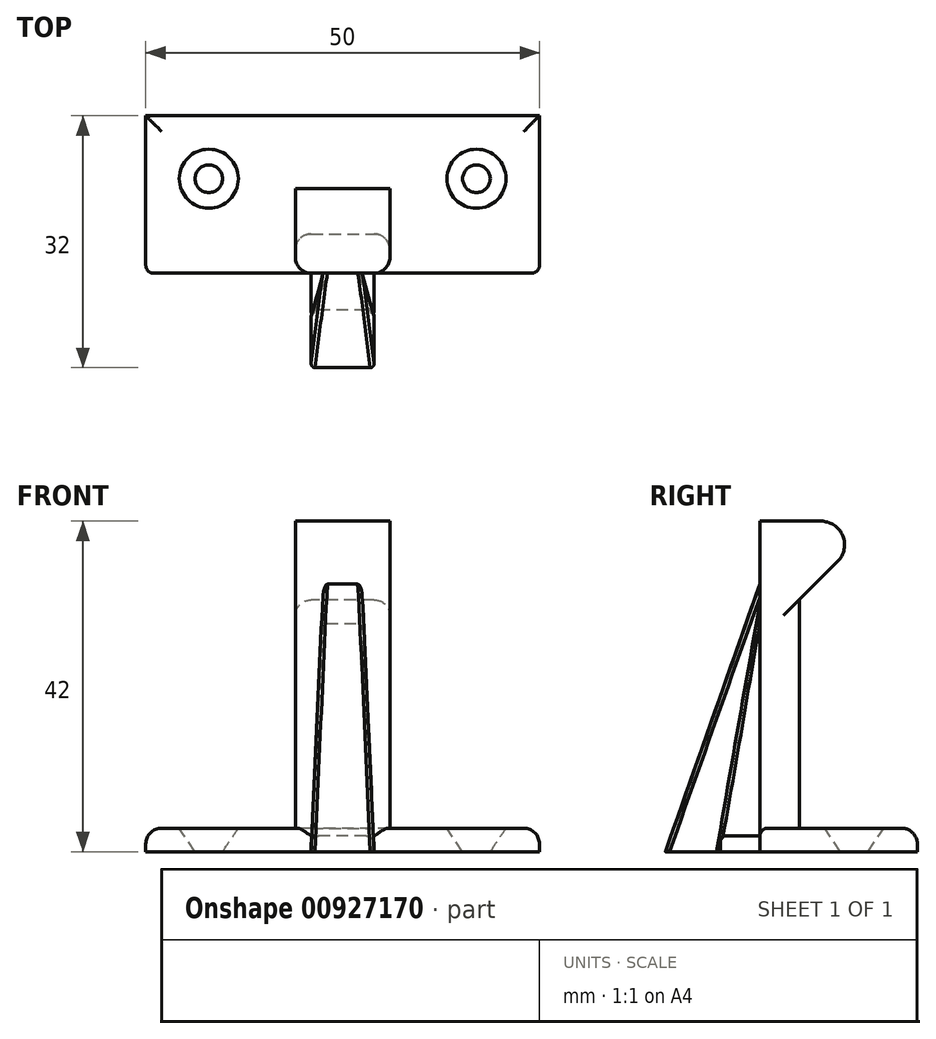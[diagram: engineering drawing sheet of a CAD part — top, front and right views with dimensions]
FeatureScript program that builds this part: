
annotation { "Feature Type Name" : "Feature", "Feature Type Description" : "" }
export const myFeature = defineFeature(function(context is Context, id is Id, definition is map)
    precondition{}
    {
        {
            var Q0;
            Q0=qCreatedBy(makeId("Top.planeOp"),FACE);
            var sketch = newSketch(context, id + "F0", { "sketchPlane" : qUnion([Q0])});
            skLineSegment(sketch, "E0.bottom", {"start": v(25, -10) * mm, "end": v(-25, -10) * mm});
            skLineSegment(sketch, "E0.top", {"start": v(25, 10) * mm, "end": v(-25, 10) * mm});
            skLineSegment(sketch, "E0.left", {"start": v(25, -10) * mm, "end": v(25, 10) * mm});
            skLineSegment(sketch, "E0.right", {"start": v(-25, -10) * mm, "end": v(-25, 10) * mm});
            skPoint(sketch, "E0.middle", {"position": v(0, 0) * mm});
            skLineSegment(sketch, "E1.bottom", {"start": v(-6, -10) * mm, "end": v(6, -10) * mm});
            skLineSegment(sketch, "E1.top", {"start": v(-6, -5) * mm, "end": v(6, -5) * mm});
            skLineSegment(sketch, "E1.left", {"start": v(6, -10) * mm, "end": v(6, -5) * mm});
            skLineSegment(sketch, "E1.right", {"start": v(-6, -10) * mm, "end": v(-6, -5) * mm});
            skPoint(sketch, "E2", {"position": v(0, -5) * mm});
            skCircle(sketch, "E3", {"center": v(-17, 2) * mm, "radius": 1.75 * mm});
            skCircle(sketch, "E4.MirrorC", {"center": v(17, 2) * mm, "radius": 1.75 * mm});
            skLineSegment(sketch, "E5.bottom", {"start": v(-4, -10) * mm, "end": v(4, -10) * mm});
            skLineSegment(sketch, "E5.top", {"start": v(-4, -22) * mm, "end": v(4, -22) * mm});
            skLineSegment(sketch, "E5.left", {"start": v(-4, -10) * mm, "end": v(-4, -22) * mm});
            skLineSegment(sketch, "E5.right", {"start": v(4, -10) * mm, "end": v(4, -22) * mm});
            skPoint(sketch, "E6", {"position": v(0, -10) * mm});
            skLineSegment(sketch, "E7", {"start": v(4, -15) * mm, "end": v(-4, -15) * mm});
            skSolve(sketch);
        }
        {
            var Q0;
            Q0=makeQuery(id+"F0.imprint","IMPRINT",FACE,{"disambiguationData":[TD([[makeQuery(id+"F0.imprint","IMPRINT",EDGE,{"derivedFrom":sQuery(id+"F0.wireOp",EDGE,"E0.top")}),1.0]])]});
            extrude(context, id + "F1", {"entities" : qUnion([Q0]), "depth" : 3 * mm, "offsetDistance" : 25 * mm});
        }
        {
            var Q0;
            Q0=makeQuery(id+"F0.imprint","IMPRINT",FACE,{"disambiguationData":[TD([[makeQuery(id+"F0.imprint","IMPRINT",EDGE,{"derivedFrom":sQuery(id+"F0.wireOp",EDGE,"E1.top")}),-1.0]])]});
            extrude(context, id + "F2", {"entities" : qUnion([Q0]), "operationType" : NewBodyOperationType.ADD, "depth" : 42 * mm, "offsetDistance" : 25 * mm});
        }
        {
            var Q0;
            {var subQ0=sQuery(id+"F0.wireOp",EDGE,"E0.bottom");Q0=makeQuery(id+"F2.boolean.opBoolean","MERGE",FACE,{"derivedFrom":[makeQuery(id+"F1.opExtrude","SWEPT_FACE",FACE,{"disambiguationData":[OSD([subQ0]),TDD([makeQuery(id+"F0.imprint","IMPRINT",EDGE,{"disambiguationData":[TD([[makeQuery(id+"F0.imprint","INTERSECT",VERTEX,{"derivedFrom":[subQ0,sQuery(id+"F0.wireOp",EDGE,"E1.right")]}),-1.0]])],"derivedFrom":subQ0})])]}),makeQuery(id+"F1.opExtrude","SWEPT_FACE",FACE,{"disambiguationData":[OSD([subQ0]),TDD([makeQuery(id+"F0.imprint","IMPRINT",EDGE,{"disambiguationData":[TD([[makeQuery(id+"F0.imprint","INTERSECT",VERTEX,{"derivedFrom":[subQ0,sQuery(id+"F0.wireOp",EDGE,"E0.left")]}),-1.0]])],"derivedFrom":subQ0})])]}),makeQuery(id+"F2.opExtrude","SWEPT_FACE",FACE,{"disambiguationData":[OSD([subQ0])]})]});}
            var sketch = newSketch(context, id + "F3", { "sketchPlane" : qUnion([Q0])});
            skLineSegment(sketch, "E8.bottom", {"start": v(-2.5, 34) * mm, "end": v(2.5, 34) * mm});
            skLineSegment(sketch, "E8.top", {"start": v(-2.5, 29) * mm, "end": v(2.5, 29) * mm});
            skLineSegment(sketch, "E8.left", {"start": v(-2.5, 34) * mm, "end": v(-2.5, 29) * mm});
            skLineSegment(sketch, "E8.right", {"start": v(2.5, 34) * mm, "end": v(2.5, 29) * mm});
            skLineSegment(sketch, "E9", {"start": v(0, 42) * mm, "end": v(0, 34) * mm, "construction": true});
            skSolve(sketch);
        }
        {
            var Q0;
            {var subQ5=sQuery(id+"F0.wireOp",EDGE,"E7");Q0=makeQuery(id+"F0.imprint","IMPRINT",FACE,{"disambiguationData":[TD([[makeQuery(id+"F0.imprint","IMPRINT",EDGE,{"derivedFrom":subQ5}),-1.0]])]});}
            extrude(context, id + "F4", {"entities" : qUnion([Q0]), "operationType" : NewBodyOperationType.ADD, "depth" : 2 * mm, "offsetDistance" : 25 * mm});
        }
        {
            var Q1;
            {var subQ0=sQuery(id+"F0.wireOp",EDGE,"E5.top");Q1=makeQuery(id+"F0.imprint","IMPRINT",FACE,{"disambiguationData":[TD([[makeQuery(id+"F0.imprint","IMPRINT",EDGE,{"derivedFrom":subQ0}),1.0]])]});}
            var Q2;
            Q2=makeQuery(id+"F3.imprint","IMPRINT",FACE,{"disambiguationData":[TD([[makeQuery(id+"F3.imprint","IMPRINT",EDGE,{"derivedFrom":sQuery(id+"F3.wireOp",EDGE,"E8.bottom")}),-1.0]])]});
            loft(context, id + "F5", {"operationType" : NewBodyOperationType.ADD, "sheetProfilesArray" : [{ "sheetProfileEntities" : qUnion([Q1]) }, { "sheetProfileEntities" : qUnion([Q2]) }]});
        }
        {
            var Q0;
            Q0=makeQuery(id+"F2.opExtrude","SWEPT_FACE",FACE,{"disambiguationData":[OSD([sQuery(id+"F0.wireOp",EDGE,"E1.top")])]});
            var sketch = newSketch(context, id + "F6", { "sketchPlane" : qUnion([Q0])});
            skLineSegment(sketch, "E10", {"start": v(-6, 32) * mm, "end": v(6, 32) * mm});
            skSolve(sketch);
        }
        {
            var Q0;
            {var subQ0=sQuery(id+"F6.wireOp",EDGE,"E10");Q0=makeQuery(id+"F6.imprint","IMPRINT",FACE,{"disambiguationData":[TD([[makeQuery(id+"F6.imprint","IMPRINT",EDGE,{"derivedFrom":subQ0}),1.0]])]});}
            extrude(context, id + "F7", {"entities" : qUnion([Q0]), "operationType" : NewBodyOperationType.ADD, "depth" : 10 * mm, "offsetDistance" : 25 * mm});
        }
        {
            var Q0;
            Q0=makeQuery(id+"F7.opExtrude","CAP_EDGE",EDGE,{"disambiguationData":[OSD([sQuery(id+"F6.wireOp",EDGE,"E10")])],"isStart":false});
            chamfer(context, id + "F8", {"entities" : qUnion([Q0]), "width" : 10 * mm, "tangentPropagation" : true});
        }
        {
            var Q0;
            Q0=makeQuery(id+"F1.opExtrude","CAP_EDGE",EDGE,{"disambiguationData":[OSD([sQuery(id+"F0.wireOp",EDGE,"E3")])],"isStart":false});
            var Q1;
            Q1=makeQuery(id+"F1.opExtrude","CAP_EDGE",EDGE,{"disambiguationData":[OSD([sQuery(id+"F0.wireOp",EDGE,"E4.MirrorC")])],"isStart":false});
            chamfer(context, id + "F9", {"entities" : qUnion([Q0, Q1]), "chamferType" : ChamferType.TWO_OFFSETS, "width1" : 3 * mm, "oppositeDirection" : false, "width2" : 2 * mm, "tangentPropagation" : true});
        }
        {
            var Q0;
            {var subQ0=sQuery(id+"F0.wireOp",EDGE,"E1.top");Q0=makeQuery(id+"F8.opChamfer","BLEND_EDGE",EDGE,{"blendedFrom":[makeQuery(id+"F7.opExtrude","CAP_EDGE",EDGE,{"disambiguationData":[OSD([sQuery(id+"F6.wireOp",EDGE,"E10")])],"isStart":false}),makeQuery(id+"F7.boolean.opBoolean","MERGE",FACE,{"derivedFrom":[makeQuery(id+"F2.opExtrude","CAP_FACE",FACE,{"disambiguationData":[OSD([sQuery(id+"F0.wireOp",EDGE,"E0.bottom"),subQ0,sQuery(id+"F0.wireOp",EDGE,"E1.left"),sQuery(id+"F0.wireOp",EDGE,"E1.right")])],"isStart":false}),makeQuery(id+"F7.opExtrude","SWEPT_FACE",FACE,{"disambiguationData":[OSD([subQ0])]})]})],"blendedInto":[makeQuery(id+"F7.boolean.opBoolean","MERGE",FACE,{"derivedFrom":[makeQuery(id+"F2.opExtrude","CAP_FACE",FACE,{"disambiguationData":[OSD([sQuery(id+"F0.wireOp",EDGE,"E0.bottom"),subQ0,sQuery(id+"F0.wireOp",EDGE,"E1.left"),sQuery(id+"F0.wireOp",EDGE,"E1.right")])],"isStart":false}),makeQuery(id+"F7.opExtrude","SWEPT_FACE",FACE,{"disambiguationData":[OSD([subQ0])]})]})]});}
            fillet(context, id + "F10", {"entities" : qUnion([Q0]), "radius" : 3 * mm, "tangentPropagation" : true, "allowEdgeOverflow" : false});
        }
        {
            var Q0;
            Q0=makeQuery(id+"F2.opExtrude","SWEPT_EDGE",EDGE,{"disambiguationData":[OSD([sQuery(id+"F0.wireOp",EDGE,"E1.top"),sQuery(id+"F0.wireOp",EDGE,"E1.left")])]});
            var Q1;
            Q1=makeQuery(id+"F2.opExtrude","SWEPT_EDGE",EDGE,{"disambiguationData":[OSD([sQuery(id+"F0.wireOp",EDGE,"E1.top"),sQuery(id+"F0.wireOp",EDGE,"E1.right")])]});
            var Q2;
            Q2=makeQuery(id+"F2.opExtrude","SWEPT_EDGE",EDGE,{"disambiguationData":[OSD([sQuery(id+"F0.wireOp",EDGE,"E0.bottom"),sQuery(id+"F0.wireOp",EDGE,"E1.left")])]});
            var Q3;
            Q3=makeQuery(id+"F2.opExtrude","SWEPT_EDGE",EDGE,{"disambiguationData":[OSD([sQuery(id+"F0.wireOp",EDGE,"E0.bottom"),sQuery(id+"F0.wireOp",EDGE,"E1.right")])]});
            fillet(context, id + "F11", {"entities" : qUnion([Q0, Q1, Q2, Q3]), "radius" : 2 * mm, "tangentPropagation" : true, "allowEdgeOverflow" : false});
        }
        {
            var Q0;
            Q0=makeQuery(id+"F1.opExtrude","CAP_EDGE",EDGE,{"disambiguationData":[OSD([sQuery(id+"F0.wireOp",EDGE,"E0.top")])],"isStart":false});
            var Q1;
            Q1=makeQuery(id+"F1.opExtrude","CAP_EDGE",EDGE,{"disambiguationData":[OSD([sQuery(id+"F0.wireOp",EDGE,"E0.right")])],"isStart":false});
            var Q2;
            Q2=makeQuery(id+"F1.opExtrude","CAP_EDGE",EDGE,{"disambiguationData":[OSD([sQuery(id+"F0.wireOp",EDGE,"E0.left")])],"isStart":false});
            fillet(context, id + "F12", {"entities" : qUnion([Q0, Q1, Q2]), "radius" : 2 * mm, "tangentPropagation" : true, "allowEdgeOverflow" : false});
        }
        {
            var Q0;
            {var subQ0=sQuery(id+"F0.wireOp",EDGE,"E0.bottom");Q0=makeQuery(id+"F1.opExtrude","CAP_EDGE",EDGE,{"disambiguationData":[OSD([subQ0]),TDD([makeQuery(id+"F0.imprint","IMPRINT",EDGE,{"disambiguationData":[TD([[makeQuery(id+"F0.imprint","INTERSECT",VERTEX,{"derivedFrom":[subQ0,sQuery(id+"F0.wireOp",EDGE,"E1.right")]}),-1.0]])],"derivedFrom":subQ0})])],"isStart":false});}
            var Q1;
            {var subQ0=sQuery(id+"F0.wireOp",EDGE,"E0.bottom");Q1=makeQuery(id+"F1.opExtrude","CAP_EDGE",EDGE,{"disambiguationData":[OSD([subQ0]),TDD([makeQuery(id+"F0.imprint","IMPRINT",EDGE,{"disambiguationData":[TD([[makeQuery(id+"F0.imprint","INTERSECT",VERTEX,{"derivedFrom":[subQ0,sQuery(id+"F0.wireOp",EDGE,"E0.left")]}),-1.0]])],"derivedFrom":subQ0})])],"isStart":false});}
            fillet(context, id + "F13", {"entities" : qUnion([Q0, Q1]), "radius" : 1 * mm, "tangentPropagation" : true, "allowEdgeOverflow" : false});
        }
        {
            var Q0;
            Q0=makeQuery(id+"F4.opExtrude","CAP_EDGE",EDGE,{"disambiguationData":[OSD([sQuery(id+"F0.wireOp",EDGE,"E5.right")])],"isStart":false});
            var Q1;
            Q1=makeQuery(id+"F4.opExtrude","CAP_EDGE",EDGE,{"disambiguationData":[OSD([sQuery(id+"F0.wireOp",EDGE,"E5.left")])],"isStart":false});
            fillet(context, id + "F14", {"entities" : qUnion([Q0, Q1]), "radius" : 1 * mm, "tangentPropagation" : true, "allowEdgeOverflow" : false});
        }
        {
            var Q0;
            Q0=makeQuery(id+"F5.opLoft","SWEPT_EDGE",EDGE,{"disambiguationData":[OSD([sQuery(id+"F0.wireOp",EDGE,"E5.right"),sQuery(id+"F0.wireOp",EDGE,"E7"),sQuery(id+"F3.wireOp",EDGE,"E8.top"),sQuery(id+"F3.wireOp",EDGE,"E8.right")])]});
            var Q1;
            Q1=makeQuery(id+"F5.opLoft","SWEPT_EDGE",EDGE,{"disambiguationData":[OSD([sQuery(id+"F0.wireOp",EDGE,"E5.left"),sQuery(id+"F0.wireOp",EDGE,"E7"),sQuery(id+"F3.wireOp",EDGE,"E8.top"),sQuery(id+"F3.wireOp",EDGE,"E8.left")])]});
            fillet(context, id + "F15", {"entities" : qUnion([Q0, Q1]), "radius" : 0.5 * mm, "tangentPropagation" : true, "allowEdgeOverflow" : false});
        }
        {
            var Q0;
            Q0=makeQuery(id+"F5.opLoft","SWEPT_EDGE",EDGE,{"disambiguationData":[OSD([sQuery(id+"F0.wireOp",EDGE,"E5.top"),sQuery(id+"F0.wireOp",EDGE,"E5.left"),sQuery(id+"F3.wireOp",EDGE,"E8.bottom"),sQuery(id+"F3.wireOp",EDGE,"E8.left")])]});
            var Q1;
            Q1=makeQuery(id+"F5.opLoft","SWEPT_EDGE",EDGE,{"disambiguationData":[OSD([sQuery(id+"F0.wireOp",EDGE,"E5.top"),sQuery(id+"F0.wireOp",EDGE,"E5.right"),sQuery(id+"F3.wireOp",EDGE,"E8.bottom"),sQuery(id+"F3.wireOp",EDGE,"E8.right")])]});
            fillet(context, id + "F16", {"entities" : qUnion([Q0, Q1]), "radius" : 0.5 * mm, "tangentPropagation" : true, "allowEdgeOverflow" : false});
        }
    });
